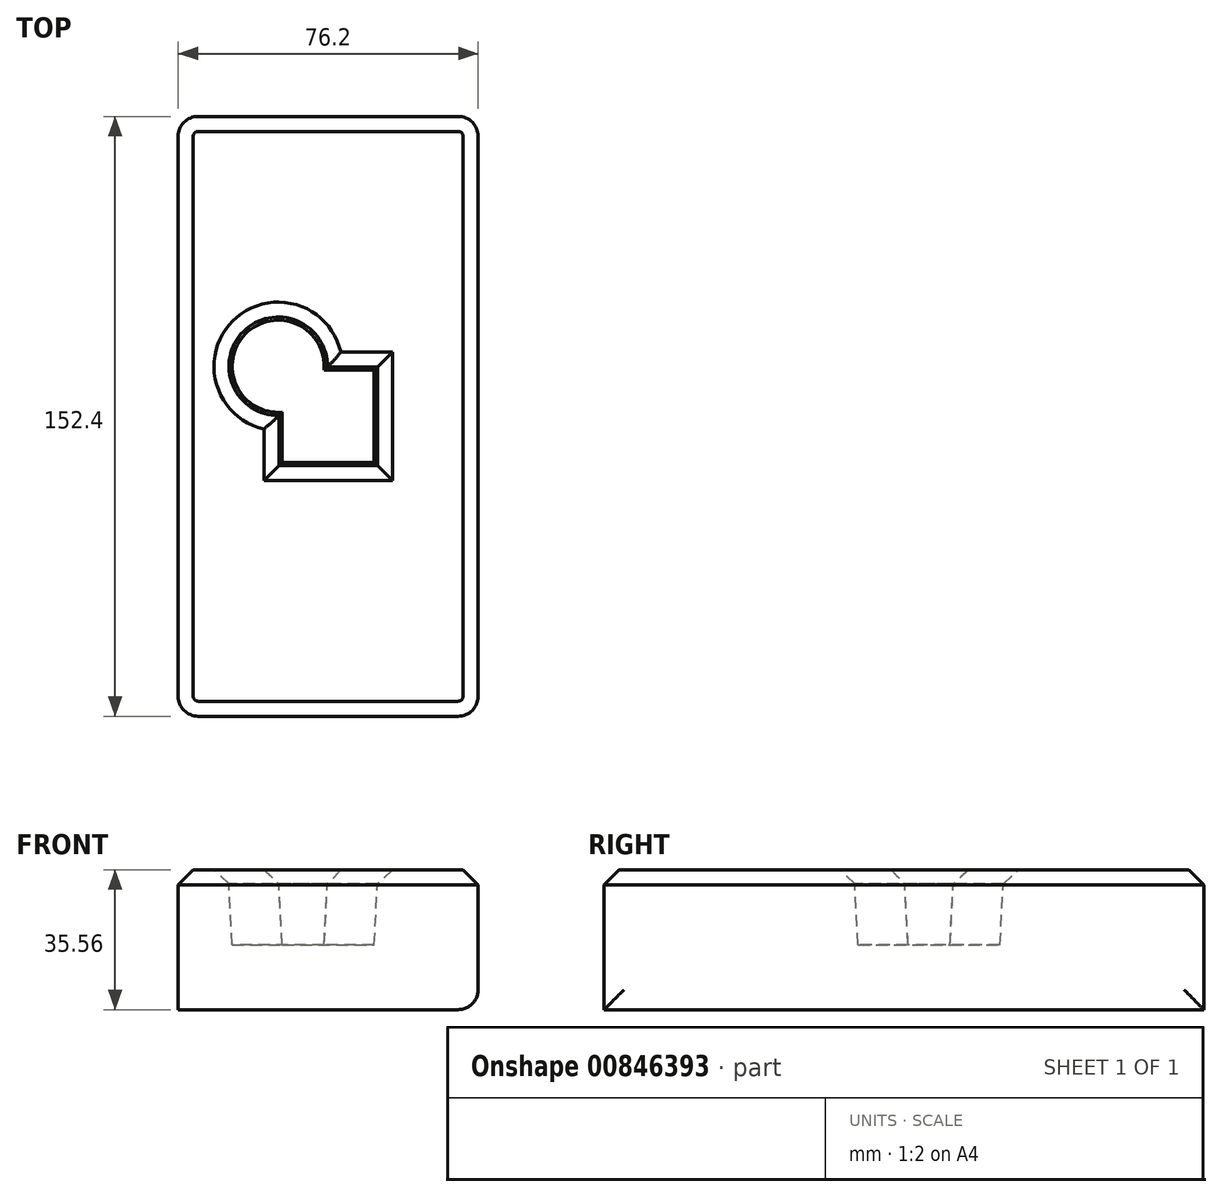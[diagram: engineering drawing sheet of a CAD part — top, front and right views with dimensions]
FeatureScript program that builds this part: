
annotation { "Feature Type Name" : "Feature", "Feature Type Description" : "" }
export const myFeature = defineFeature(function(context is Context, id is Id, definition is map)
    precondition{}
    {
        {
            var Q0;
            Q0=qCreatedBy(makeId("Front.planeOp"),FACE);
            var sketch = newSketch(context, id + "F0", { "sketchPlane" : qUnion([Q0])});
            skLineSegment(sketch, "E0.bottom", {"start": v(0, 0) * mm, "end": v(76.2, 0) * mm});
            skLineSegment(sketch, "E0.top", {"start": v(0, 35.56) * mm, "end": v(76.2, 35.56) * mm});
            skLineSegment(sketch, "E0.left", {"start": v(0, 0) * mm, "end": v(0, 35.56) * mm});
            skLineSegment(sketch, "E0.right", {"start": v(76.2, 0) * mm, "end": v(76.2, 35.56) * mm});
            skSolve(sketch);
        }
        {
            var Q0;
            Q0=makeQuery(id+"F0.imprint","IMPRINT",FACE,{"disambiguationData":[TD([[makeQuery(id+"F0.imprint","IMPRINT",EDGE,{"derivedFrom":sQuery(id+"F0.wireOp",EDGE,"E0.bottom")}),1.0]])]});
            extrude(context, id + "F1", {"entities" : qUnion([Q0]), "depth" : 152.4 * mm, "offsetDistance" : 25.4 * mm});
        }
        {
            var Q0;
            Q0=makeQuery(id+"F1.opExtrude","SWEPT_FACE",FACE,{"disambiguationData":[OSD([sQuery(id+"F0.wireOp",EDGE,"E0.top")])]});
            var sketch = newSketch(context, id + "F2", { "sketchPlane" : qUnion([Q0])});
            skArc(sketch, "E1", {"start": v(38.1, -63.5) * mm, "mid": v(16.42, -54.52) * mm, "end": v(25.4, -76.2) * mm});
            skLineSegment(sketch, "E2", {"start": v(38.1, -63.5) * mm, "end": v(50.8, -63.5) * mm});
            skLineSegment(sketch, "E3", {"start": v(50.8, -63.5) * mm, "end": v(50.8, -88.9) * mm});
            skLineSegment(sketch, "E4", {"start": v(50.8, -88.9) * mm, "end": v(25.4, -88.9) * mm});
            skLineSegment(sketch, "E5", {"start": v(25.4, -88.9) * mm, "end": v(25.4, -76.2) * mm});
            skSolve(sketch);
        }
        {
            var Q0;
            Q0=makeQuery(id+"F2.imprint","IMPRINT",FACE,{"disambiguationData":[TD([[makeQuery(id+"F2.imprint","IMPRINT",EDGE,{"derivedFrom":sQuery(id+"F2.wireOp",EDGE,"E1")}),1.0]])]});
            extrude(context, id + "F3", {"entities" : qUnion([Q0]), "operationType" : NewBodyOperationType.REMOVE, "oppositeDirection" : true, "depth" : 19.05 * mm, "offsetDistance" : 25.4 * mm, "hasDraft" : true, "draftAngle" : 3 * degree, "draftPullDirection" : true});
        }
        {
            var Q0;
            Q0=makeQuery(id+"F1.opExtrude","CAP_EDGE",EDGE,{"disambiguationData":[OSD([sQuery(id+"F0.wireOp",EDGE,"E0.right")])],"isStart":false});
            var Q1;
            Q1=makeQuery(id+"F1.opExtrude","SWEPT_EDGE",EDGE,{"disambiguationData":[OSD([sQuery(id+"F0.wireOp",EDGE,"E0.bottom"),sQuery(id+"F0.wireOp",EDGE,"E0.right")])]});
            var Q2;
            Q2=makeQuery(id+"F1.opExtrude","CAP_EDGE",EDGE,{"disambiguationData":[OSD([sQuery(id+"F0.wireOp",EDGE,"E0.right")])],"isStart":true});
            var Q3;
            Q3=makeQuery(id+"F1.opExtrude","CAP_EDGE",EDGE,{"disambiguationData":[OSD([sQuery(id+"F0.wireOp",EDGE,"E0.left")])],"isStart":true});
            var Q4;
            Q4=makeQuery(id+"F1.opExtrude","CAP_EDGE",EDGE,{"disambiguationData":[OSD([sQuery(id+"F0.wireOp",EDGE,"E0.left")])],"isStart":false});
            fillet(context, id + "F4", {"entities" : qUnion([Q0, Q1, Q2, Q3, Q4]), "radius" : 5.08 * mm, "tangentPropagation" : true, "allowEdgeOverflow" : false});
        }
        {
            var Q0;
            Q0=makeQuery(id+"F1.opExtrude","SWEPT_FACE",FACE,{"disambiguationData":[OSD([sQuery(id+"F0.wireOp",EDGE,"E0.top")])]});
            chamfer(context, id + "F5", {"entities" : qUnion([Q0]), "width" : 3.8 * mm, "tangentPropagation" : true});
        }
    });
